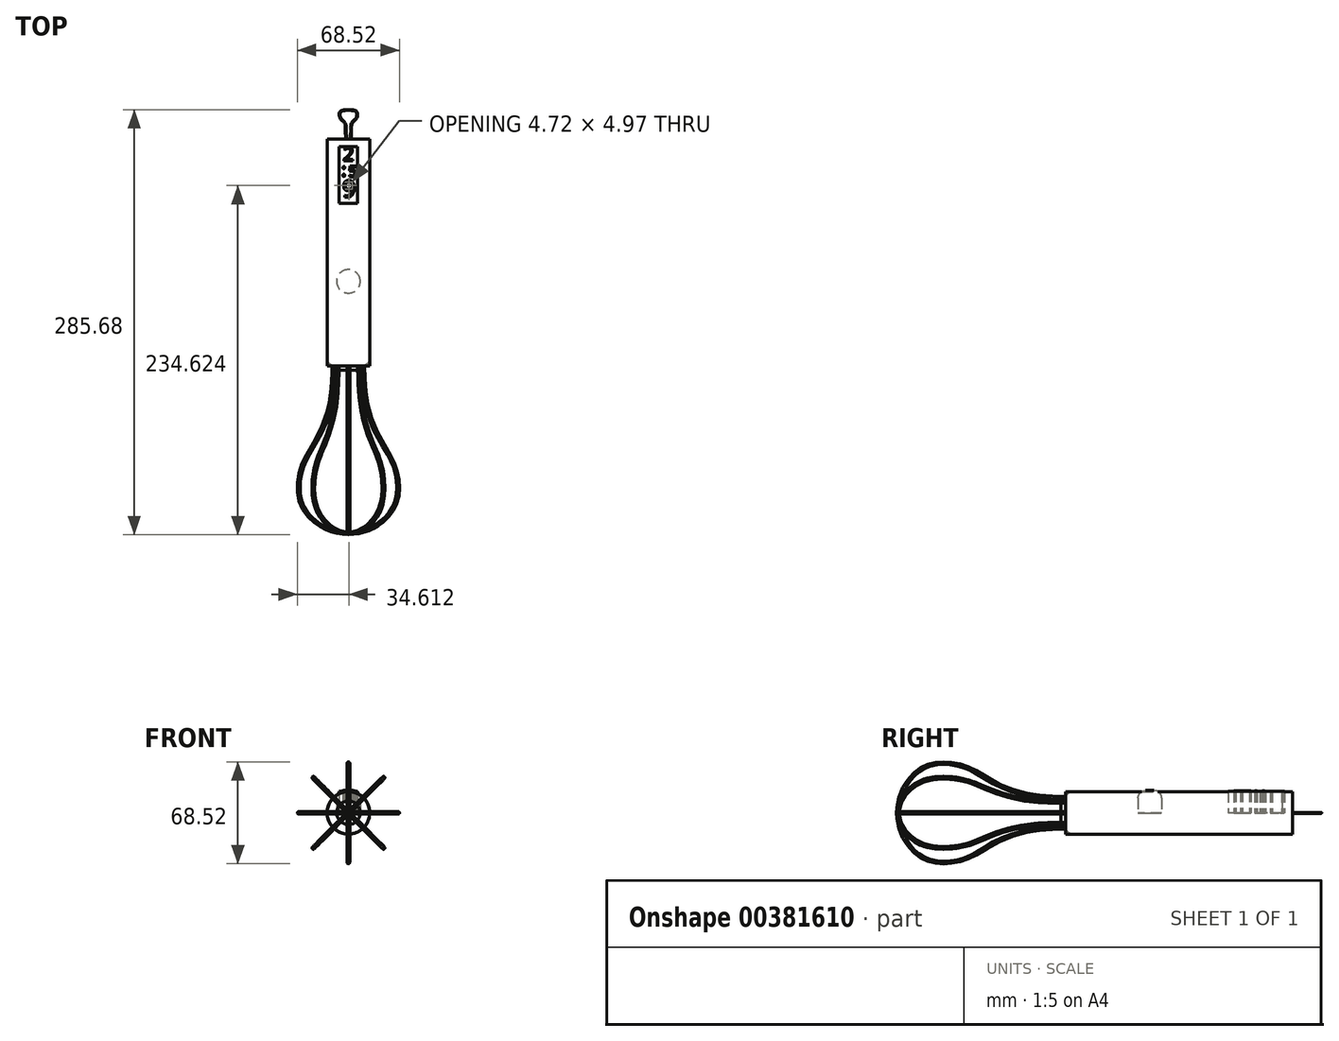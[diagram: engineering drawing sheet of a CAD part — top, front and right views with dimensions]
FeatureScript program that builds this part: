
annotation { "Feature Type Name" : "Feature", "Feature Type Description" : "" }
export const myFeature = defineFeature(function(context is Context, id is Id, definition is map)
    precondition{}
    {
        {
            var Q0;
            Q0=qCreatedBy(makeId("Front.planeOp"),FACE);
            var sketch = newSketch(context, id + "F0", { "sketchPlane" : qUnion([Q0])});
            skCircle(sketch, "E0", {"center": v(0, 0) * mm, "radius": 14.27 * mm});
            skSolve(sketch);
        }
        {
            var Q0;
            Q0=makeQuery(id+"F0.imprint","IMPRINT",FACE,{"disambiguationData":[TD([[makeQuery(id+"F0.imprint","IMPRINT",EDGE,{"derivedFrom":sQuery(id+"F0.wireOp",EDGE,"E0")}),1.0]])]});
            extrude(context, id + "F1", {"entities" : qUnion([Q0]), "depth" : 152.4 * mm});
        }
        {
            var Q0;
            Q0=makeQuery(id+"F1.opExtrude","CAP_FACE",FACE,{"disambiguationData":[OSD([sQuery(id+"F0.wireOp",EDGE,"E0")])],"isStart":false});
            var sketch = newSketch(context, id + "F2", { "sketchPlane" : qUnion([Q0])});
            skCircle(sketch, "E1", {"center": v(-10.11, 0) * mm, "radius": 0.91 * mm});
            skSolve(sketch);
        }
        {
            var Q0;
            Q0=qCreatedBy(makeId("Top.planeOp"),FACE);
            var sketch = newSketch(context, id + "F3", { "sketchPlane" : qUnion([Q0])});
            skFitSpline(sketch, "E2", {"points": [v(-10.11, -152.4) * mm, v(-12.72, -180.65) * mm, v(-21.89, -203.27) * mm, v(-31.06, -220.39) * mm, v(-32.28, -243) * mm, v(-23.11, -256.46) * mm, v(-10.88, -263.18) * mm, v(0, -265.02) * mm], "startDerivative": vector(-4.58, -165.66) * mm, "endDerivative": vector(99.04, -9.44) * mm});
            skSolve(sketch);
        }
        {
            var Q0;
            Q0=makeQuery(id+"F2.imprint","IMPRINT",FACE,{"disambiguationData":[TD([[makeQuery(id+"F2.imprint","IMPRINT",EDGE,{"derivedFrom":sQuery(id+"F2.wireOp",EDGE,"E1")}),1.0]])]});
            var Q1;
            Q1=sQuery(id+"F3.wireOp",EDGE,"E2");
            sweep(context, id + "F4", {"operationType" : NewBodyOperationType.ADD, "profiles" : qUnion([Q0]), "path" : qUnion([Q1])});
        }
        {
            var Q0;
            Q0=qCreatedBy(makeId("Top.planeOp"),FACE);
            var sketch = newSketch(context, id + "F5", { "sketchPlane" : qUnion([Q0])});
            skLineSegment(sketch, "E3", {"start": v(0, -3.55) * mm, "end": v(0, -265.13) * mm});
            skSolve(sketch);
        }
        {
            var Q0;
            Q0=makeQuery(id+"F1.opExtrude","SWEPT_BODY",BODY,{"disambiguationData":[OSD([sQuery(id+"F0.wireOp",EDGE,"E0")])]});
            var Q1;
            Q1=sQuery(id+"F5.wireOp",EDGE,"E3");
            circularPattern(context, id + "F6", {"entities" : qUnion([Q0]), "axis" : qUnion([Q1]), "angle" : 360 * degree, "instanceCount" : 8, "equalSpace" : true});
        }
        {
            var Q0;
            Q0=qCreatedBy(makeId("Front.planeOp"),FACE);
            var sketch = newSketch(context, id + "F7", { "sketchPlane" : qUnion([Q0])});
            skCircle(sketch, "E4", {"center": v(-1.48, 0) * mm, "radius": 0.3 * mm});
            skSolve(sketch);
        }
        {
            var Q0;
            Q0=qCreatedBy(makeId("Top.planeOp"),FACE);
            var sketch = newSketch(context, id + "F8", { "sketchPlane" : qUnion([Q0])});
            skFitSpline(sketch, "E5", {"points": [v(-1.48, 0) * mm, v(-1.83, 5.86) * mm, v(-2.2, 10.39) * mm, v(-4.66, 13.03) * mm, v(-5.8, 15.1) * mm, v(-5.6, 17.94) * mm, v(-3.15, 19.26) * mm, v(0, 19.45) * mm], "startDerivative": vector(-3.1, 32.1) * mm, "endDerivative": vector(23.24, -0.14) * mm});
            skSolve(sketch);
        }
        {
            var Q0;
            Q0=qCreatedBy(makeId("Top.planeOp"),FACE);
            var sketch = newSketch(context, id + "F9", { "sketchPlane" : qUnion([Q0])});
            skLineSegment(sketch, "E6", {"start": v(0, -152.87) * mm, "end": v(0, 19.47) * mm});
            skSolve(sketch);
        }
        {
            var Q0;
            Q0=makeQuery(id+"F7.imprint","IMPRINT",FACE,{"disambiguationData":[TD([[makeQuery(id+"F7.imprint","IMPRINT",EDGE,{"derivedFrom":sQuery(id+"F7.wireOp",EDGE,"E4")}),1.0]])]});
            var Q1;
            Q1=sQuery(id+"F8.wireOp",EDGE,"E5");
            sweep(context, id + "F10", {"profiles" : qUnion([Q0]), "path" : qUnion([Q1])});
        }
        {
            var Q0;
            Q0=makeQuery(id+"F10.opSweep","SWEPT_BODY",BODY,{"disambiguationData":[OSD([sQuery(id+"F7.wireOp",EDGE,"E4"),sQuery(id+"F8.wireOp",EDGE,"E5")])]});
            var Q1;
            Q1=sQuery(id+"F9.wireOp",EDGE,"E6");
            circularPattern(context, id + "F11", {"entities" : qUnion([Q0]), "axis" : qUnion([Q1]), "angle" : 360 * degree, "instanceCount" : 2, "equalSpace" : true});
        }
        {
            var Q0;
            Q0=qCreatedBy(makeId("Top.planeOp"),FACE);
            var sketch = newSketch(context, id + "F12", { "sketchPlane" : qUnion([Q0])});
            skLineSegment(sketch, "E7.bottom", {"start": v(-6.27, -5.18) * mm, "end": v(6.27, -5.18) * mm});
            skLineSegment(sketch, "E7.top", {"start": v(-6.27, -43.19) * mm, "end": v(6.27, -43.19) * mm});
            skLineSegment(sketch, "E7.left", {"start": v(-6.27, -5.18) * mm, "end": v(-6.27, -43.19) * mm});
            skLineSegment(sketch, "E7.right", {"start": v(6.27, -5.18) * mm, "end": v(6.27, -43.19) * mm});
            skPoint(sketch, "E7.middle", {"position": v(0, -24.18) * mm});
            skSolve(sketch);
        }
        {
            var Q0;
            Q0 = qSketchRegion(id + "F12", true);
            extrude(context, id + "F13", {"entities" : qUnion([Q0]), "depth" : 14.48 * mm});
        }
        {
            var Q0;
            Q0=qCreatedBy(makeId("Top.planeOp"),FACE);
            var sketch = newSketch(context, id + "F14", { "sketchPlane" : qUnion([Q0])});
            skText(sketch, "E8", { "text": "2", "fontName": "OpenSans-Regular.ttf"});
            const initialGuessF14  = {"E8": [-0.00356, -0.01464, 1, 0, 0.00906]};
            skSetInitialGuess(sketch, initialGuessF14);
            skSolve(sketch);
        }
        {
            var Q0;
            Q0 = qSketchRegion(id + "F14", true);
            extrude(context, id + "F15", {"entities" : qUnion([Q0]), "depth" : 14.48 * mm});
        }
        {
            var Q0;
            Q0=qCreatedBy(makeId("Top.planeOp"),FACE);
            var sketch = newSketch(context, id + "F16", { "sketchPlane" : qUnion([Q0])});
            skText(sketch, "E9", { "text": ":", "fontName": "OpenSans-Regular.ttf"});
            const initialGuessF16  = {"E9": [-0.00466, -0.02499, 1, 0, 0.00854]};
            skSetInitialGuess(sketch, initialGuessF16);
            skSolve(sketch);
        }
        {
            var Q0;
            Q0 = qSketchRegion(id + "F16", true);
            extrude(context, id + "F17", {"entities" : qUnion([Q0]), "depth" : 14.73 * mm});
        }
        {
            var Q0;
            Q0=qCreatedBy(makeId("Top.planeOp"),FACE);
            var sketch = newSketch(context, id + "F18", { "sketchPlane" : qUnion([Q0])});
            skText(sketch, "E10", { "text": "5", "fontName": "OpenSans-Regular.ttf"});
            const initialGuessF18  = {"E10": [0, -0.0253, 1, 0, 0.0073]};
            skSetInitialGuess(sketch, initialGuessF18);
            skSolve(sketch);
        }
        {
            var Q0;
            Q0 = qSketchRegion(id + "F18", true);
            extrude(context, id + "F19", {"entities" : qUnion([Q0]), "depth" : 14.48 * mm});
        }
        {
            var Q0;
            Q0=qCreatedBy(makeId("Top.planeOp"),FACE);
            var sketch = newSketch(context, id + "F20", { "sketchPlane" : qUnion([Q0])});
            skText(sketch, "E11", { "text": "9", "fontName": "OpenSans-Regular.ttf"});
            const initialGuessF20  = {"E11": [-0.00405, -0.03897, 1, 0, 0.01116]};
            skSetInitialGuess(sketch, initialGuessF20);
            skSolve(sketch);
        }
        {
            var Q0;
            Q0 = qSketchRegion(id + "F20", true);
            extrude(context, id + "F21", {"entities" : qUnion([Q0]), "depth" : 14.73 * mm});
        }
        {
            var Q0;
            Q0=qCreatedBy(makeId("Top.planeOp"),FACE);
            var sketch = newSketch(context, id + "F22", { "sketchPlane" : qUnion([Q0])});
            skCircle(sketch, "E12", {"center": v(0, -95.65) * mm, "radius": 7.92 * mm});
            skSolve(sketch);
        }
        {
            var Q0;
            Q0 = qSketchRegion(id + "F22", true);
            extrude(context, id + "F23", {"entities" : qUnion([Q0]), "depth" : 15 * mm});
        }
        {
            var Q0;
            Q0=makeQuery(id+"F23.opExtrude","CAP_EDGE",EDGE,{"disambiguationData":[OSD([sQuery(id+"F22.wireOp",EDGE,"E12")])],"isStart":false});
            fillet(context, id + "F24", {"entities" : qUnion([Q0]), "radius" : 5.08 * mm, "tangentPropagation" : true, "allowEdgeOverflow" : false});
        }
        {
            var Q0;
            Q0=makeQuery(id+"F2.imprint","IMPRINT",FACE,{"disambiguationData":[TD([[makeQuery(id+"F2.imprint","IMPRINT",EDGE,{"derivedFrom":sQuery(id+"F2.wireOp",EDGE,"E1")}),-1.0]])]});
            var sketch = newSketch(context, id + "F25", { "sketchPlane" : qUnion([Q0])});
            skCircle(sketch, "E13", {"center": v(0, 0) * mm, "radius": 7.92 * mm});
            skSolve(sketch);
        }
        {
            var Q0;
            Q0 = qSketchRegion(id + "F25", true);
            extrude(context, id + "F26", {"entities" : qUnion([Q0]), "depth" : 3.05 * mm});
        }
        {
            var Q0;
            Q0=makeQuery(id+"F1.opExtrude","CAP_EDGE",EDGE,{"disambiguationData":[OSD([sQuery(id+"F0.wireOp",EDGE,"E0")])],"isStart":false});
            fillet(context, id + "F27", {"entities" : qUnion([Q0]), "radius" : 5.08 * mm, "tangentPropagation" : true, "allowEdgeOverflow" : false});
        }
    });
